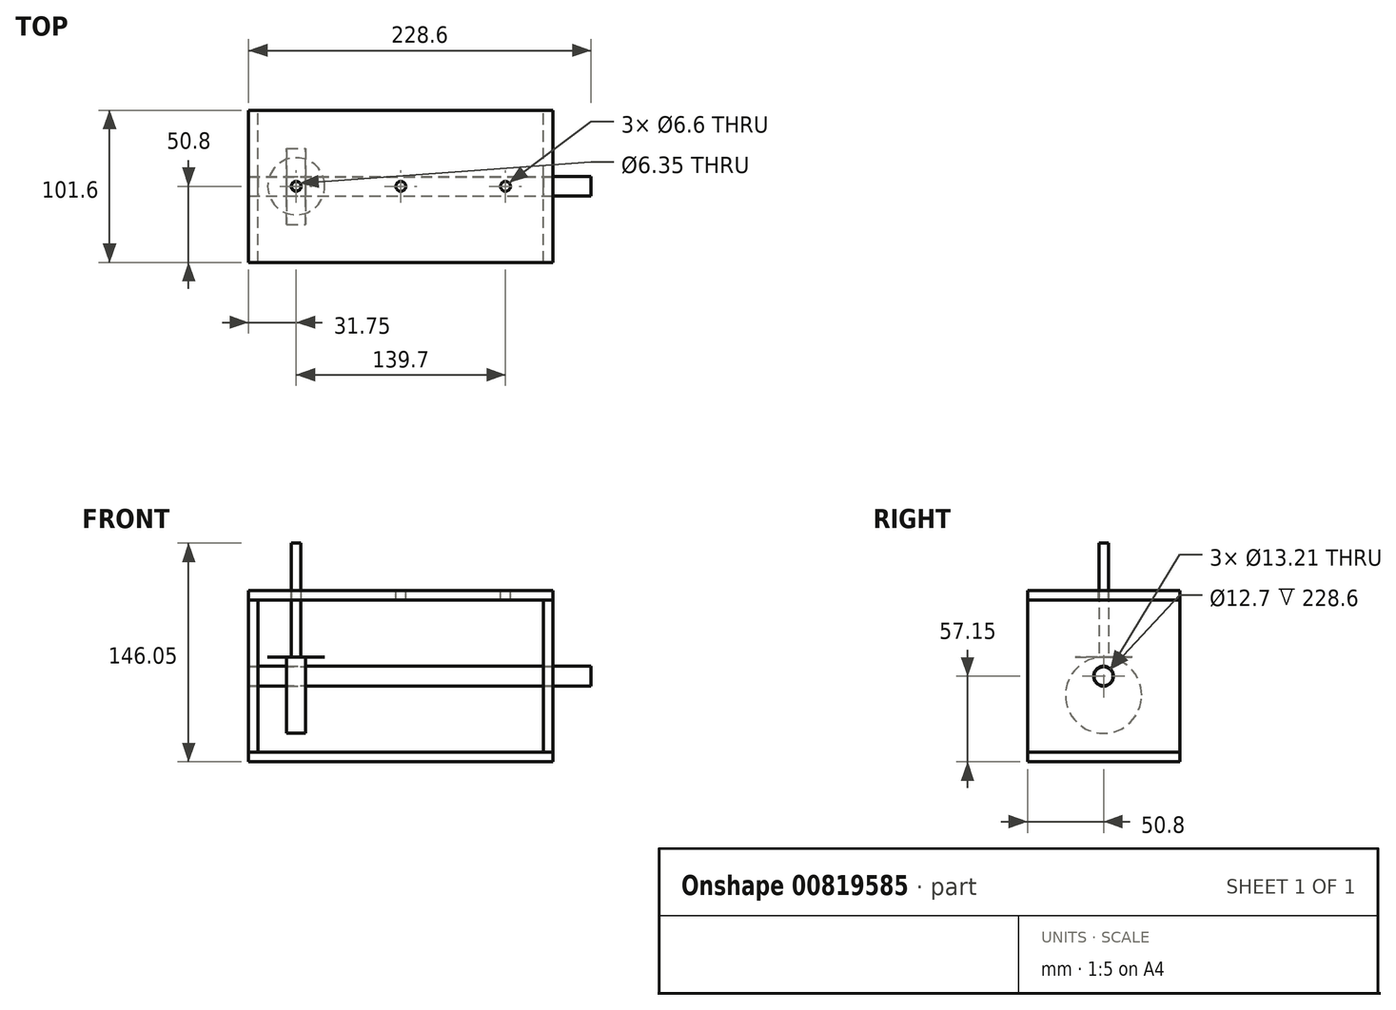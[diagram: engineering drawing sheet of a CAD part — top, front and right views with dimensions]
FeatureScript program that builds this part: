
annotation { "Feature Type Name" : "Feature", "Feature Type Description" : "" }
export const myFeature = defineFeature(function(context is Context, id is Id, definition is map)
    precondition{}
    {
        {
            var Q0;
            Q0=qCreatedBy(makeId("Front.planeOp"),FACE);
            var sketch = newSketch(context, id + "F0", { "sketchPlane" : qUnion([Q0])});
            skLineSegment(sketch, "E0", {"start": v(-101.6, 0) * mm, "end": v(101.6, 0) * mm});
            skLineSegment(sketch, "E1", {"start": v(-101.6, 0) * mm, "end": v(-101.6, 114.3) * mm});
            skLineSegment(sketch, "E2", {"start": v(-101.6, 114.3) * mm, "end": v(101.6, 114.3) * mm});
            skLineSegment(sketch, "E3", {"start": v(101.6, 0) * mm, "end": v(101.6, 114.3) * mm});
            skLineSegment(sketch, "E4", {"start": v(101.6, 107.95) * mm, "end": v(-101.6, 107.95) * mm});
            skLineSegment(sketch, "E5", {"start": v(101.6, 6.35) * mm, "end": v(-101.6, 6.35) * mm});
            skLineSegment(sketch, "E6", {"start": v(101.6, 57.15) * mm, "end": v(95.25, 57.15) * mm, "construction": true});
            skLineSegment(sketch, "E7", {"start": v(0, 114.3) * mm, "end": v(0, 107.95) * mm, "construction": true});
            skLineSegment(sketch, "E8", {"start": v(0, 6.35) * mm, "end": v(0, 0) * mm, "construction": true});
            skLineSegment(sketch, "E9", {"start": v(-95.25, 57.15) * mm, "end": v(-101.6, 57.15) * mm, "construction": true});
            skLineSegment(sketch, "E10", {"start": v(-95.25, 107.95) * mm, "end": v(-95.25, 6.35) * mm});
            skLineSegment(sketch, "E11", {"start": v(95.25, 107.95) * mm, "end": v(95.25, 6.35) * mm});
            skLineSegment(sketch, "E12.bottom", {"start": v(76.2, 88.9) * mm, "end": v(63.5, 88.9) * mm});
            skLineSegment(sketch, "E12.top", {"start": v(76.2, 38.1) * mm, "end": v(63.5, 38.1) * mm});
            skLineSegment(sketch, "E12.left", {"start": v(76.2, 88.9) * mm, "end": v(76.2, 38.1) * mm});
            skLineSegment(sketch, "E12.right", {"start": v(63.5, 88.9) * mm, "end": v(63.5, 38.1) * mm});
            skLineSegment(sketch, "E13.bottom", {"start": v(6.35, 88.9) * mm, "end": v(-6.35, 88.9) * mm});
            skLineSegment(sketch, "E13.top", {"start": v(6.35, 38.1) * mm, "end": v(-6.35, 38.1) * mm});
            skLineSegment(sketch, "E13.left", {"start": v(6.35, 88.9) * mm, "end": v(6.35, 38.1) * mm});
            skLineSegment(sketch, "E13.right", {"start": v(-6.35, 88.9) * mm, "end": v(-6.35, 38.1) * mm});
            skLineSegment(sketch, "E14", {"start": v(76.2, 63.5) * mm, "end": v(63.5, 63.5) * mm});
            skLineSegment(sketch, "E15", {"start": v(6.35, 63.5) * mm, "end": v(-6.35, 63.5) * mm});
            skLineSegment(sketch, "E16", {"start": v(-63.5, 44.45) * mm, "end": v(-76.2, 44.45) * mm});
            skLineSegment(sketch, "E17", {"start": v(95.25, 57.15) * mm, "end": v(-95.25, 57.15) * mm});
            skLineSegment(sketch, "E18", {"start": v(69.85, 57.15) * mm, "end": v(69.85, 63.5) * mm, "construction": true});
            skPoint(sketch, "E18.startSnap0", {"position": v(69.85, 63.5) * mm});
            skPoint(sketch, "E19.startSnap0", {"position": v(0, 63.5) * mm});
            skLineSegment(sketch, "E20", {"start": v(-69.85, 44.45) * mm, "end": v(-69.85, 57.15) * mm, "construction": true});
            skLineSegment(sketch, "E21", {"start": v(0, 63.5) * mm, "end": v(0, 57.15) * mm, "construction": true});
            skLineSegment(sketch, "E22", {"start": v(-69.85, 69.85) * mm, "end": v(-69.85, 146.05) * mm, "construction": true});
            skLineSegment(sketch, "E23", {"start": v(0, 88.9) * mm, "end": v(0, 165.1) * mm, "construction": true});
            skLineSegment(sketch, "E24", {"start": v(69.85, 88.9) * mm, "end": v(69.85, 165.1) * mm, "construction": true});
            skLineSegment(sketch, "E25.bottom", {"start": v(-76.2, 69.85) * mm, "end": v(-63.5, 69.85) * mm});
            skLineSegment(sketch, "E25.top", {"start": v(-76.2, 19.05) * mm, "end": v(-63.5, 19.05) * mm});
            skLineSegment(sketch, "E25.left", {"start": v(-76.2, 69.85) * mm, "end": v(-76.2, 19.05) * mm});
            skLineSegment(sketch, "E25.right", {"start": v(-63.5, 69.85) * mm, "end": v(-63.5, 19.05) * mm});
            skSolve(sketch);
        }
        {
            var Q0;
            {var subQ1=sQuery(id+"F0.wireOp",EDGE,"E2");Q0=makeQuery(id+"F0.imprint","IMPRINT",FACE,{"disambiguationData":[TD([[makeQuery(id+"F0.imprint","IMPRINT",EDGE,{"derivedFrom":subQ1}),-1.0]])]});}
            var Q1;
            {var subQ4=sQuery(id+"F0.wireOp",EDGE,"E0");Q1=makeQuery(id+"F0.imprint","IMPRINT",FACE,{"disambiguationData":[TD([[makeQuery(id+"F0.imprint","IMPRINT",EDGE,{"derivedFrom":subQ4}),1.0]])]});}
            extrude(context, id + "F1", {"entities" : qUnion([Q0, Q1]), "endBound" : BoundingType.SYMMETRIC, "depth" : 101.6 * mm, "offsetDistance" : 25.4 * mm});
        }
        {
            var Q0;
            {var subQ1=sQuery(id+"F0.wireOp",EDGE,"E4");var subQ5=sQuery(id+"F0.wireOp",EDGE,"E1");var subQ8=makeQuery(id+"F0.imprint","INTERSECT",VERTEX,{"derivedFrom":[subQ5,subQ1]});Q0=makeQuery(id+"F0.imprint","IMPRINT",FACE,{"disambiguationData":[TD([[makeQuery(id+"F0.imprint","IMPRINT",EDGE,{"disambiguationData":[TD([[subQ8,1.0]])],"derivedFrom":subQ5}),-1.0]])]});}
            var Q1;
            {var subQ0=sQuery(id+"F0.wireOp",EDGE,"E4");var subQ1=sQuery(id+"F0.wireOp",EDGE,"E3");var subQ2=makeQuery(id+"F0.imprint","INTERSECT",VERTEX,{"derivedFrom":[subQ1,subQ0]});Q1=makeQuery(id+"F0.imprint","IMPRINT",FACE,{"disambiguationData":[TD([[makeQuery(id+"F0.imprint","IMPRINT",EDGE,{"disambiguationData":[TD([[subQ2,1.0]])],"derivedFrom":subQ1}),1.0]])]});}
            var Q2;
            Q2=makeQuery(id+"F1.opExtrude","CAP_FACE",FACE,{"disambiguationData":[OSD([sQuery(id+"F0.wireOp",EDGE,"E1"),sQuery(id+"F0.wireOp",EDGE,"E2"),sQuery(id+"F0.wireOp",EDGE,"E3"),sQuery(id+"F0.wireOp",EDGE,"E4")])],"isStart":false});
            var Q3;
            Q3=makeQuery(id+"F1.opExtrude","CAP_FACE",FACE,{"disambiguationData":[OSD([sQuery(id+"F0.wireOp",EDGE,"E0"),sQuery(id+"F0.wireOp",EDGE,"E1"),sQuery(id+"F0.wireOp",EDGE,"E3"),sQuery(id+"F0.wireOp",EDGE,"E5")])],"isStart":true});
            extrude(context, id + "F2", {"entities" : qUnion([Q0, Q1]), "endBound" : BoundingType.UP_TO_SURFACE, "depth" : 25.4 * mm, "endBoundEntityFace" : qUnion([Q2]), "offsetDistance" : 25.4 * mm, "hasSecondDirection" : true, "secondDirectionBound" : SecondDirectionBoundingType.UP_TO_SURFACE, "secondDirectionOppositeDirection" : true, "secondDirectionDepth" : 25.4 * mm, "secondDirectionBoundEntityFace" : qUnion([Q3])});
        }
        {
            var Q0;
            {var subQ0=sQuery(id+"F0.wireOp",EDGE,"E16");Q0=makeQuery(id+"F0.imprint","IMPRINT",FACE,{"disambiguationData":[TD([[makeQuery(id+"F0.imprint","IMPRINT",EDGE,{"derivedFrom":subQ0}),1.0]])]});}
            var Q1;
            Q1=sQuery(id+"F0.wireOp",EDGE,"E16");
            revolve(context, id + "F3", {"surfaceOperationType" : NewSurfaceOperationType.NEW, "entities" : qUnion([Q0]), "axis" : qUnion([Q1]), "revolveType" : RevolveType.FULL});
        }
        {
            var Q0;
            Q0=makeQuery(id+"F2.opExtrude","SWEPT_FACE",FACE,{"disambiguationData":[OSD([sQuery(id+"F0.wireOp",EDGE,"E3")])]});
            var sketch = newSketch(context, id + "F4", { "sketchPlane" : qUnion([Q0])});
            skCircle(sketch, "E26", {"center": v(0, 57.15) * mm, "radius": 6.35 * mm});
            skCircle(sketch, "E27", {"center": v(0, 57.15) * mm, "radius": 6.6 * mm});
            skSolve(sketch);
        }
        {
            var Q0;
            Q0=makeQuery(id+"F4.imprint","IMPRINT",FACE,{"disambiguationData":[TD([[makeQuery(id+"F4.imprint","IMPRINT",EDGE,{"derivedFrom":sQuery(id+"F4.wireOp",EDGE,"E26")}),-1.0]])]});
            var Q1;
            Q1=makeQuery(id+"F4.imprint","IMPRINT",FACE,{"disambiguationData":[TD([[makeQuery(id+"F4.imprint","IMPRINT",EDGE,{"derivedFrom":sQuery(id+"F4.wireOp",EDGE,"E26")}),1.0]])]});
            extrude(context, id + "F5", {"entities" : qUnion([Q0, Q1]), "operationType" : NewBodyOperationType.REMOVE, "endBound" : BoundingType.THROUGH_ALL, "oppositeDirection" : true, "depth" : 25.4 * mm, "offsetDistance" : 25.4 * mm});
        }
        {
            var Q0;
            Q0=makeQuery(id+"F4.imprint","IMPRINT",FACE,{"disambiguationData":[TD([[makeQuery(id+"F4.imprint","IMPRINT",EDGE,{"derivedFrom":sQuery(id+"F4.wireOp",EDGE,"E26")}),-1.0]])]});
            var Q1;
            Q1=makeQuery(id+"F2.opExtrude","SWEPT_FACE",FACE,{"disambiguationData":[OSD([sQuery(id+"F0.wireOp",EDGE,"E1")])]});
            extrude(context, id + "F6", {"entities" : qUnion([Q0]), "endBound" : BoundingType.UP_TO_SURFACE, "oppositeDirection" : true, "depth" : 25.4 * mm, "endBoundEntityFace" : qUnion([Q1]), "offsetDistance" : 25.4 * mm, "hasSecondDirection" : true, "secondDirectionOppositeDirection" : false, "secondDirectionDepth" : 25.4 * mm});
        }
        {
            var Q0;
            Q0=makeQuery(id+"F6.opExtrude","SWEPT_BODY",BODY,{"disambiguationData":[OSD([sQuery(id+"F4.wireOp",EDGE,"E26")])]});
            var Q1;
            Q1=makeQuery(id+"F3.opRevolve","SWEPT_BODY",BODY,{"disambiguationData":[OSD([sQuery(id+"F0.wireOp",EDGE,"7YLZPD0O-fxV0-EZ8k-YRh1-LoM9O4BxGDj8.top"),sQuery(id+"F0.wireOp",EDGE,"7YLZPD0O-fxV0-EZ8k-YRh1-LoM9O4BxGDj8.left"),sQuery(id+"F0.wireOp",EDGE,"7YLZPD0O-fxV0-EZ8k-YRh1-LoM9O4BxGDj8.right"),sQuery(id+"F0.wireOp",EDGE,"E16")])]});
            booleanBodies(context, id + "F7", {"operationType" : BooleanOperationType.SUBTRACTION, "tools" : qUnion([Q0]), "targets" : qUnion([Q1]), "keepTools" : true});
        }
        {
            var Q0;
            Q0=qCreatedBy(makeId("Top.planeOp"),FACE);
            var Q1;
            Q1=sQuery(id+"F0.wireOp",VERTEX,"E22.start");
            cPlane(context, id + "F8", {"entities" : qUnion([Q0, Q1]), "cplaneType" : CPlaneType.PLANE_POINT, "offset" : 25.4 * mm, "width" : 152.4 * mm, "height" : 152.4 * mm});
        }
        {
            var Q0;
            Q0=qCreatedBy(id+"F8.planeOp",FACE);
            var sketch = newSketch(context, id + "F9", { "sketchPlane" : qUnion([Q0])});
            skCircle(sketch, "E28", {"center": v(-69.85, 0) * mm, "radius": 3.18 * mm});
            skCircle(sketch, "E29", {"center": v(-69.85, 0) * mm, "radius": 19.05 * mm});
            skSolve(sketch);
        }
        {
            var Q0;
            Q0=makeQuery(id+"F1.opExtrude","SWEPT_FACE",FACE,{"disambiguationData":[OSD([sQuery(id+"F0.wireOp",EDGE,"E2")])]});
            var sketch = newSketch(context, id + "F10", { "sketchPlane" : qUnion([Q0])});
            skPoint(sketch, "E30", {"position": v(-69.85, 0) * mm});
            skPoint(sketch, "E31", {"position": v(0, 0) * mm});
            skPoint(sketch, "E32", {"position": v(69.85, 0) * mm});
            skSolve(sketch);
        }
        {
            var Q0;
            Q0=sQuery(id+"F10.wireOp",VERTEX,"E30");
            var Q1;
            Q1=sQuery(id+"F10.wireOp",VERTEX,"E31");
            var Q2;
            Q2=sQuery(id+"F10.wireOp",VERTEX,"E32");
            var Q3;
            Q3=makeQuery(id+"F1.opExtrude","SWEPT_BODY",BODY,{"disambiguationData":[OSD([sQuery(id+"F0.wireOp",EDGE,"E1"),sQuery(id+"F0.wireOp",EDGE,"E2"),sQuery(id+"F0.wireOp",EDGE,"E3"),sQuery(id+"F0.wireOp",EDGE,"E4")])]});
            hole(context, id + "F11", {"style" : HoleStyle.SIMPLE, "endStyle" : HoleEndStyle.THROUGH, "holeDiameter" : 6.6 * mm, "majorDiameter" : 6.35 * mm, "isTappedThrough" : true, "tappedDepth" : 12.7 * mm, "tapClearance" : 3, "locations" : qUnion([Q0, Q1, Q2]), "scope" : qUnion([Q3])});
        }
        {
            var Q0;
            Q0=makeQuery(id+"F9.imprint","IMPRINT",FACE,{"disambiguationData":[TD([[makeQuery(id+"F9.imprint","IMPRINT",EDGE,{"derivedFrom":sQuery(id+"F9.wireOp",EDGE,"E28")}),1.0]])]});
            var Q1;
            Q1=sQuery(id+"F0.wireOp",VERTEX,"E22.end");
            extrude(context, id + "F12", {"entities" : qUnion([Q0]), "endBound" : BoundingType.UP_TO_VERTEX, "depth" : 25.4 * mm, "endBoundEntityVertex" : qUnion([Q1]), "offsetDistance" : 25.4 * mm});
        }
        {
            var Q0;
            Q0=makeQuery(id+"F9.imprint","IMPRINT",FACE,{"disambiguationData":[TD([[makeQuery(id+"F9.imprint","IMPRINT",EDGE,{"derivedFrom":sQuery(id+"F9.wireOp",EDGE,"E28")}),-1.0]])]});
            extrude(context, id + "F13", {"entities" : qUnion([Q0]), "depth" : 1 / 203.2 * mm, "offsetDistance" : 25.4 * mm});
        }
    });
